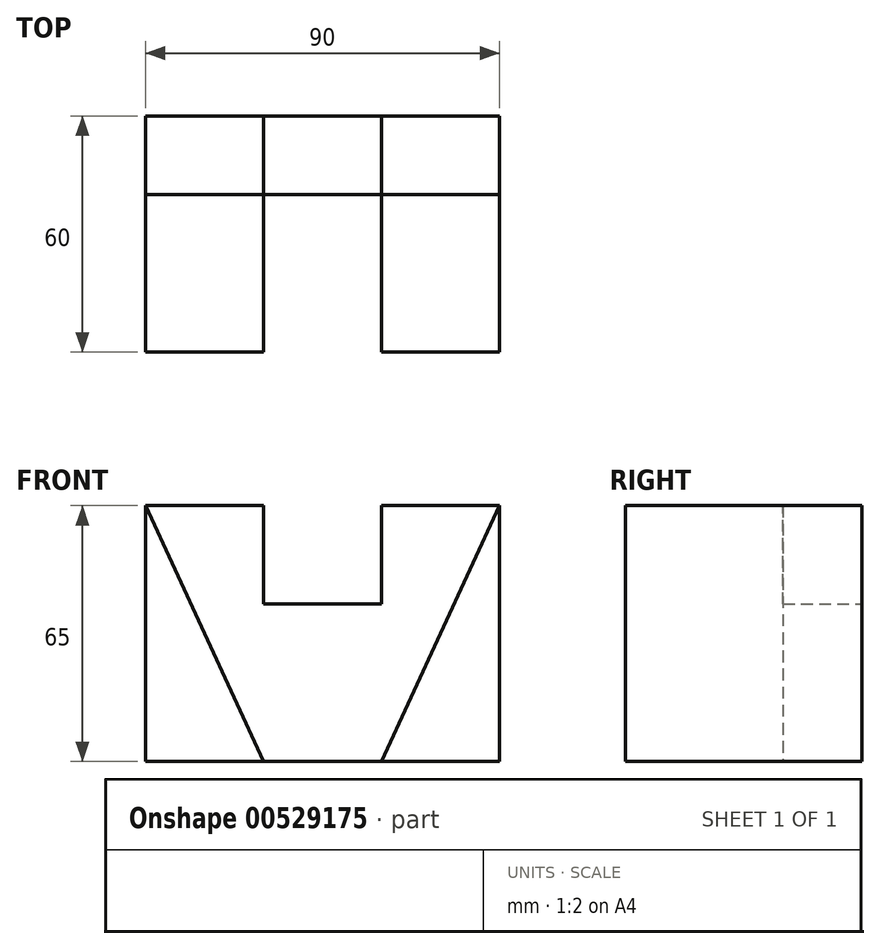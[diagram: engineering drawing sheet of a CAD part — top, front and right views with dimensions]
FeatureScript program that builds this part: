
annotation { "Feature Type Name" : "Feature", "Feature Type Description" : "" }
export const myFeature = defineFeature(function(context is Context, id is Id, definition is map)
    precondition{}
    {
        {
            var Q0;
            Q0=qCreatedBy(makeId("Front.planeOp"),FACE);
            var sketch = newSketch(context, id + "F0", { "sketchPlane" : qUnion([Q0])});
            skLineSegment(sketch, "E0.bottom", {"start": v(15, 20) * mm, "end": v(-15, 20) * mm});
            skLineSegment(sketch, "E0.top", {"start": v(15, -20) * mm, "end": v(-15, -20) * mm});
            skLineSegment(sketch, "E0.left", {"start": v(15, 20) * mm, "end": v(15, -20) * mm});
            skLineSegment(sketch, "E0.right", {"start": v(-15, 20) * mm, "end": v(-15, -20) * mm});
            skPoint(sketch, "E0.middle", {"position": v(0, 0) * mm});
            skLineSegment(sketch, "E1.bottom", {"start": v(15, -20) * mm, "end": v(45, -20) * mm});
            skLineSegment(sketch, "E1.top", {"start": v(15, 45) * mm, "end": v(45, 45) * mm});
            skLineSegment(sketch, "E1.left", {"start": v(15, -20) * mm, "end": v(15, 45) * mm});
            skLineSegment(sketch, "E1.right", {"start": v(45, -20) * mm, "end": v(45, 45) * mm});
            skLineSegment(sketch, "E2.bottom", {"start": v(-15, -20) * mm, "end": v(-45, -20) * mm});
            skLineSegment(sketch, "E2.top", {"start": v(-15, 45) * mm, "end": v(-45, 45) * mm});
            skLineSegment(sketch, "E2.left", {"start": v(-15, -20) * mm, "end": v(-15, 45) * mm});
            skLineSegment(sketch, "E2.right", {"start": v(-45, -20) * mm, "end": v(-45, 45) * mm});
            skSolve(sketch);
        }
        {
            var Q0;
            Q0 = qSketchRegion(id + "F0", true);
            extrude(context, id + "F1", {"entities" : qUnion([Q0]), "depth" : 20 * mm, "offsetDistance" : 25 * mm});
        }
        {
            var Q0;
            Q0=makeQuery(id+"F1.opExtrude","CAP_FACE",FACE,{"disambiguationData":[OSD([sQuery(id+"F0.wireOp",EDGE,"E0.bottom"),sQuery(id+"F0.wireOp",EDGE,"E0.top"),sQuery(id+"F0.wireOp",EDGE,"E1.bottom"),sQuery(id+"F0.wireOp",EDGE,"E1.top"),sQuery(id+"F0.wireOp",EDGE,"E1.left"),sQuery(id+"F0.wireOp",EDGE,"E1.right"),sQuery(id+"F0.wireOp",EDGE,"E2.bottom"),sQuery(id+"F0.wireOp",EDGE,"E2.top"),sQuery(id+"F0.wireOp",EDGE,"E2.left"),sQuery(id+"F0.wireOp",EDGE,"E2.right")])],"isStart":false});
            var sketch = newSketch(context, id + "F2", { "sketchPlane" : qUnion([Q0])});
            skLineSegment(sketch, "E3", {"start": v(-45, 45) * mm, "end": v(-15, -20) * mm});
            skLineSegment(sketch, "E4", {"start": v(45, 45) * mm, "end": v(15, -20) * mm});
            skPoint(sketch, "E4.endSnap0", {"position": v(15, 32.5) * mm});
            skSolve(sketch);
        }
        {
            var Q0;
            {var subQ0=sQuery(id+"F2.wireOp",EDGE,"E3");Q0=makeQuery(id+"F2.imprint","IMPRINT",FACE,{"disambiguationData":[TD([[makeQuery(id+"F2.imprint","IMPRINT",EDGE,{"derivedFrom":subQ0}),-1.0]])]});}
            var Q1;
            {var subQ0=sQuery(id+"F2.wireOp",EDGE,"E4");Q1=makeQuery(id+"F2.imprint","IMPRINT",FACE,{"disambiguationData":[TD([[makeQuery(id+"F2.imprint","IMPRINT",EDGE,{"derivedFrom":subQ0}),1.0]])]});}
            extrude(context, id + "F3", {"entities" : qUnion([Q0, Q1]), "operationType" : NewBodyOperationType.ADD, "depth" : 40 * mm, "offsetDistance" : 25 * mm});
        }
    });
